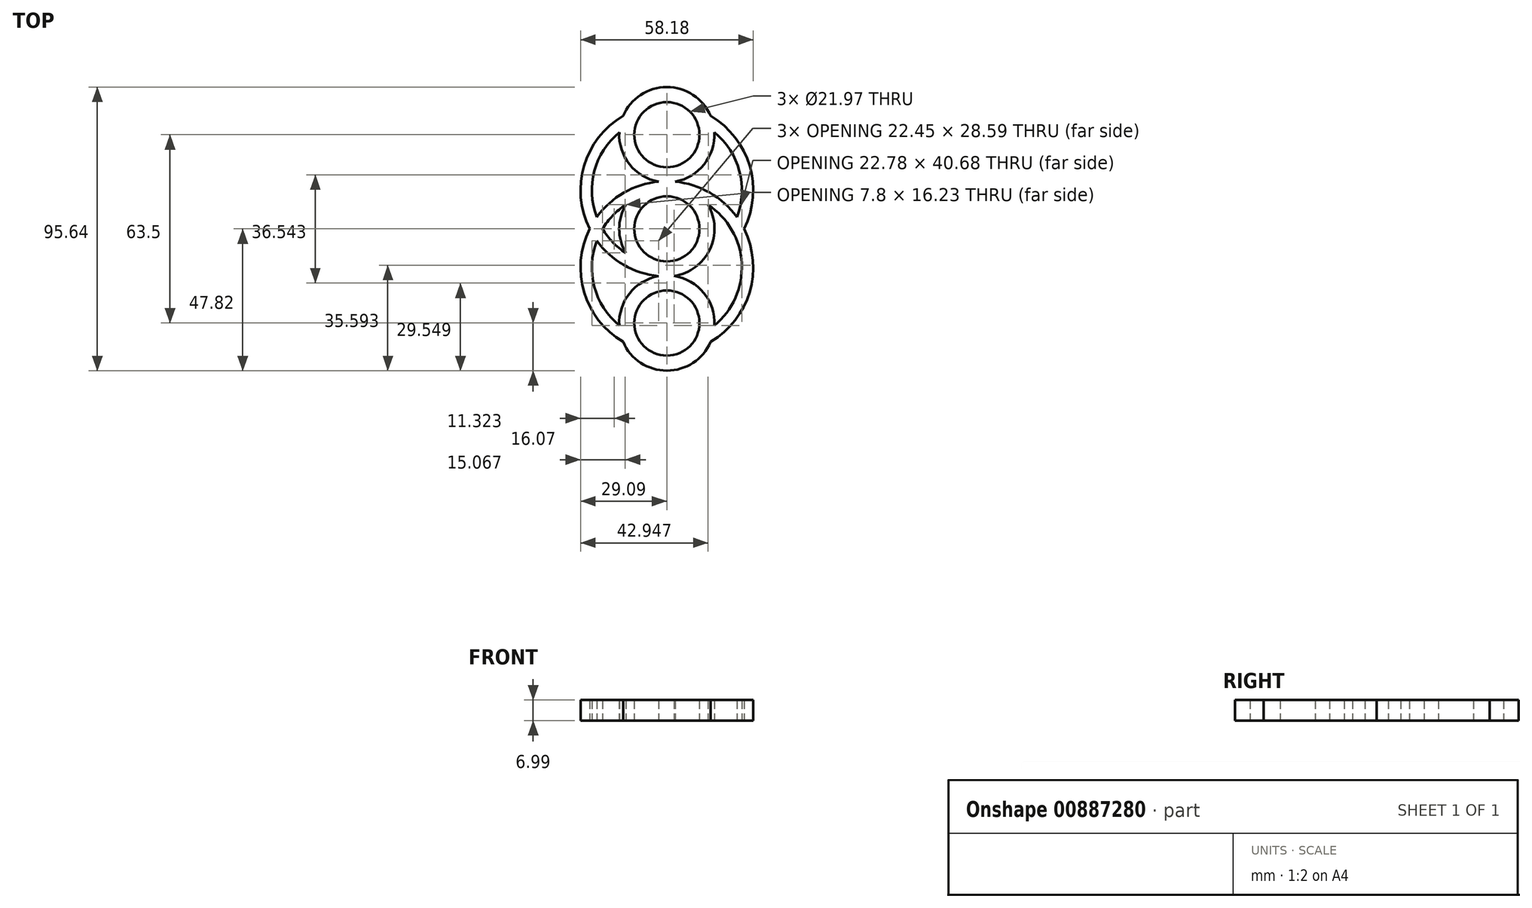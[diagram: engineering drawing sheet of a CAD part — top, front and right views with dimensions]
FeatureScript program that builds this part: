
annotation { "Feature Type Name" : "Feature", "Feature Type Description" : "" }
export const myFeature = defineFeature(function(context is Context, id is Id, definition is map)
    precondition{}
    {
        {
            var Q0;
            Q0=qCreatedBy(makeId("Top.planeOp"),FACE);
            var sketch = newSketch(context, id + "F0", { "sketchPlane" : qUnion([Q0])});
            skCircle(sketch, "E0", {"center": v(0, 0) * mm, "radius": 10.99 * mm});
            skCircle(sketch, "E1", {"center": v(0, 31.75) * mm, "radius": 10.99 * mm});
            skArc(sketch, "E2.0", {"start": v(-2.47, 15.88) * mm, "mid": v(-16.07, 0) * mm, "end": v(-2.47, -15.88) * mm});
            skArc(sketch, "E3.0", {"start": v(2.8, 15.93) * mm, "mid": v(0, 47.82) * mm, "end": v(-2.8, 15.93) * mm});
            skArc(sketch, "E4", {"start": v(-14.76, 38.1) * mm, "mid": v(-28.4, 6.74) * mm, "end": v(-2.8, -15.93) * mm});
            skArc(sketch, "E5.0", {"start": v(-16.04, 32.57) * mm, "mid": v(-25.25, 11.68) * mm, "end": v(-13.87, -8.11) * mm});
            skArc(sketch, "E6.MirrorC", {"start": v(-2.8, 15.93) * mm, "mid": v(0, 47.82) * mm, "end": v(2.8, 15.93) * mm});
            skArc(sketch, "E7.MirrorCS", {"start": v(16.04, 32.57) * mm, "mid": v(25.25, 11.68) * mm, "end": v(13.87, -8.11) * mm});
            skArc(sketch, "E8.MirrorCS", {"start": v(14.76, 38.1) * mm, "mid": v(28.4, 6.74) * mm, "end": v(2.8, -15.93) * mm});
            skPoint(sketch, "E9", {"position": v(-2.47, 15.88) * mm});
            skPoint(sketch, "E10", {"position": v(2.47, 15.88) * mm});
            skArc(sketch, "E11.MirrorCS", {"start": v(-2.47, -15.88) * mm, "mid": v(0, -47.82) * mm, "end": v(2.47, -15.88) * mm});
            skCircle(sketch, "E12.MirrorC", {"center": v(0, -31.75) * mm, "radius": 10.99 * mm});
            skArc(sketch, "E13.MirrorCS", {"start": v(-16.04, -32.57) * mm, "mid": v(-25.25, -11.68) * mm, "end": v(-13.87, 8.11) * mm});
            skArc(sketch, "E14.MirrorCS", {"start": v(-14.76, -38.1) * mm, "mid": v(-28.4, -6.74) * mm, "end": v(-2.8, 15.93) * mm});
            skArc(sketch, "E15.MirrorCS", {"start": v(16.04, -32.57) * mm, "mid": v(25.25, -11.68) * mm, "end": v(13.87, 8.11) * mm});
            skArc(sketch, "E16.MirrorCS", {"start": v(14.76, -38.1) * mm, "mid": v(28.4, -6.74) * mm, "end": v(2.8, 15.93) * mm});
            skPoint(sketch, "E17.orphan", {"position": v(0, 16.07) * mm});
            skArc(sketch, "E18.trimOffspring", {"start": v(2.47, -15.88) * mm, "mid": v(16.07, 0) * mm, "end": v(2.47, 15.87) * mm});
            skPoint(sketch, "E19.orphan", {"position": v(0, -16.07) * mm});
            skSolve(sketch);
        }
        {
            var Q0;
            Q0 = qSketchRegion(id + "F0", true);
            var Q1;
            {var subQ1=sQuery(id+"F0.wireOp",EDGE,"E2.0");var subQ5=sQuery(id+"F0.wireOp",EDGE,"E11.MirrorCS");var subQ6=makeQuery(id+"F0.imprint","INTERSECT",VERTEX,{"derivedFrom":[subQ1,subQ5]});Q1=makeQuery(id+"F0.imprint","IMPRINT",FACE,{"disambiguationData":[TD([[makeQuery(id+"F0.imprint","IMPRINT",EDGE,{"disambiguationData":[TD([[subQ6,1.0]])],"derivedFrom":subQ1}),-1.0]])]});}
            var Q2;
            {var subQ1=sQuery(id+"F0.wireOp",EDGE,"E7.MirrorCS");var subQ7=sQuery(id+"F0.wireOp",EDGE,"E18.trimOffspring");var subQ9=makeQuery(id+"F0.imprint","INTERSECT",VERTEX,{"derivedFrom":[subQ1,subQ7]});Q2=makeQuery(id+"F0.imprint","IMPRINT",FACE,{"disambiguationData":[TD([[makeQuery(id+"F0.imprint","IMPRINT",EDGE,{"disambiguationData":[TD([[subQ9,1.0]])],"derivedFrom":subQ1}),1.0]])]});}
            extrude(context, id + "F1", {"entities" : qUnion([Q0, Q1, Q2]), "depth" : 7 * mm, "offsetDistance" : 25.4 * mm});
        }
    });
